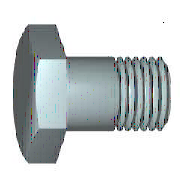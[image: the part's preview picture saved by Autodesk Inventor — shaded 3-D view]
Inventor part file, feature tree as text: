
AUTODESK INVENTOR PART (.ipt)
format: ipt  version: 2021 (Build 250183000, 183)  size: 196,608 bytes
history: native  units: mm (DEFAULTED — no unit token found)
features: sketch x3, extrude x1, chamfer x1, plane x1
ambient origin geometry x7: Origin, YZ Plane, XZ Plane, X Axis, Y Axis, Z Axis, Center Point
bodies: Solid1 (feature_tree), Body (feature_tree)
feature tree (6):
  extrude  "Head"  Depth=19.0mm
  chamfer  "Chamfer1"  Distance=9.2mm
  plane  "Work Plane1"
  sketch  "Sketch1"  dims[d0=25.0mm d1=19.0mm]
  sketch  "Sketch2"  dims[d2=16.0mm]
  sketch  "Sketch4"  dims[d12=90.0deg d3=9.2mm d4=0.0mm d5=30.0deg d21=90.0deg d6=1.2269mm d7=1.227mm d8=0.0mm d9=0.8001mm d10=22.5mm d11=24.0mm d13=1.227mm d14=16.0mm d15=19.0mm d16=0.0mm d19=24.0mm d55=45.0deg d57=0.0mm d58=0.0mm]
